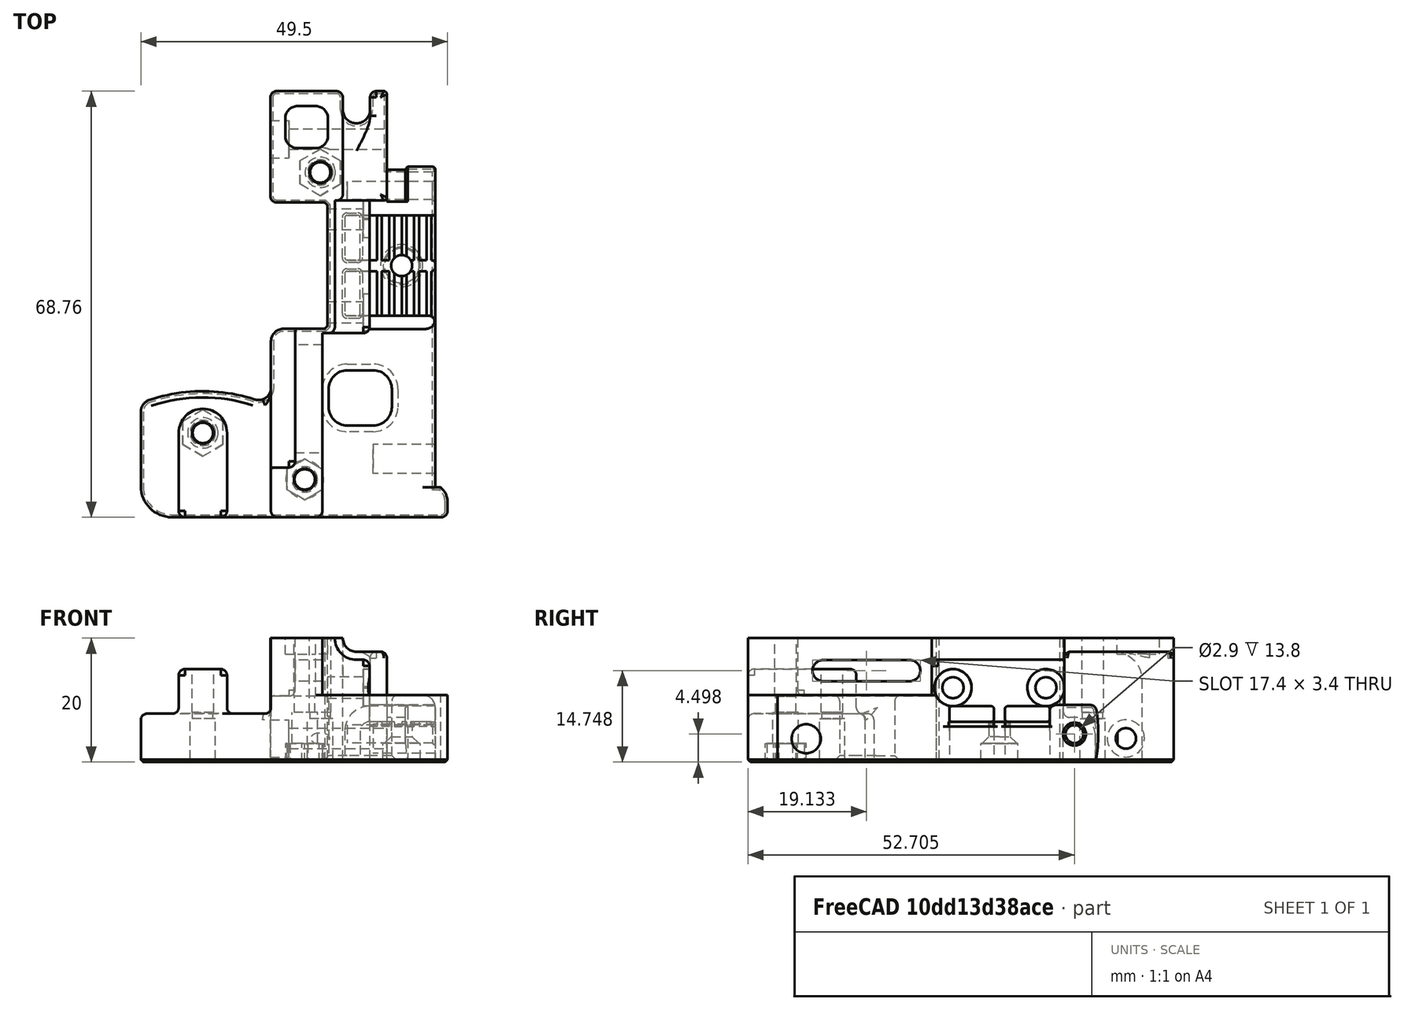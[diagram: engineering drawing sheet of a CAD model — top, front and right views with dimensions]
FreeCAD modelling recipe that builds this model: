
FCSTD DOCUMENT  (FreeCAD 0.18R16146 (Git))
Label: carrier
License: Other
LicenseURL: GPL3
objects: Part::Cylinder×9, Part::MultiFuse×4, Part::Cut×2, Part::Feature×1, Part::Chamfer×1
note: 17 computed .brp shape members not serialized (recipe doc carries the construction recipe); baked Part::Feature solids carry a one-line shape summary decoded from their .brp

FEATURE [Part::Feature] Part__Feature377001  label="COMPOUND009"
  Placement = pos=(-5,-35,20) rot=(-1,0,0;1.5708rad)
  shape: bbox 49.92 x 69.17 x 22.32 mm, 357 faces (baked)
FEATURE [Part::Cylinder] Cylinder
  Angle = 360
  AttacherType = Attacher::AttachEngine3D
  Height = 8
  Placement = pos=(-14.3,-21.395,0) rot=(0,0,1;0rad)
  Radius = 4
FEATURE [Part::Cylinder] Cylinder001
  Angle = 360
  AttacherType = Attacher::AttachEngine3D
  Height = 7.6
  Placement = pos=(2.15,-28.9,3) rot=(0,0,1;0rad)
  Radius = 4
FEATURE [Part::Cylinder] Cylinder002
  Angle = 360
  AttacherType = Attacher::AttachEngine3D
  Height = 8
  Placement = pos=(4.65,20.65,0) rot=(0,0,1;0rad)
  Radius = 4
FEATURE [Part::Cylinder] Cylinder003
  Angle = 360
  AttacherType = Attacher::AttachEngine3D
  Height = 7
  Placement = pos=(4.65,20.65,0) rot=(0,0,1;0rad)
  Radius = 2.05
FEATURE [Part::Cylinder] Cylinder004
  Angle = 360
  AttacherType = Attacher::AttachEngine3D
  Height = 5
  Placement = pos=(2.15,-28.9,3) rot=(0,0,1;0rad)
  Radius = 2.05
FEATURE [Part::Cylinder] Cylinder005
  Angle = 360
  AttacherType = Attacher::AttachEngine3D
  Height = 7
  Placement = pos=(-14.3,-21.395,0) rot=(0,0,1;0rad)
  Radius = 2.05
FEATURE [Part::Cylinder] Cylinder006
  Angle = 360
  AttacherType = Attacher::AttachEngine3D
  Height = 8
  Placement = pos=(-14.3,-21.395,0) rot=(0,0,1;0rad)
  Radius = 1.65
FEATURE [Part::Cylinder] Cylinder007
  Angle = 360
  AttacherType = Attacher::AttachEngine3D
  Height = 8
  Placement = pos=(4.65,20.65,0) rot=(0,0,1;0rad)
  Radius = 1.65
FEATURE [Part::Cylinder] Cylinder008
  Angle = 360
  AttacherType = Attacher::AttachEngine3D
  Height = 14
  Placement = pos=(2.15,-28.9,0) rot=(0,0,1;0rad)
  Radius = 1.65
FEATURE [Part::MultiFuse] Fusion005
  Shapes = -> [Cylinder003,Cylinder004,Cylinder005]
FEATURE [Part::MultiFuse] Fusion
  Shapes = -> [Cylinder002,Cylinder001,Cylinder]
FEATURE [Part::MultiFuse] Fusion006
  Shapes = -> [Part__Feature377001,Fusion]
FEATURE [Part::MultiFuse] Fusion007
  Shapes = -> [Cylinder006,Cylinder007,Cylinder008]
FEATURE [Part::Cut] Cut
  Base = -> Fusion006
  Tool = -> Fusion007
FEATURE [Part::Cut] Cut001
  Base = -> Cut
  Tool = -> Fusion005
FEATURE [Part::Chamfer] Chamfer
  Base = -> Cut001
  Edges = 2 edges r=0.4: [Edge629,Edge630]
